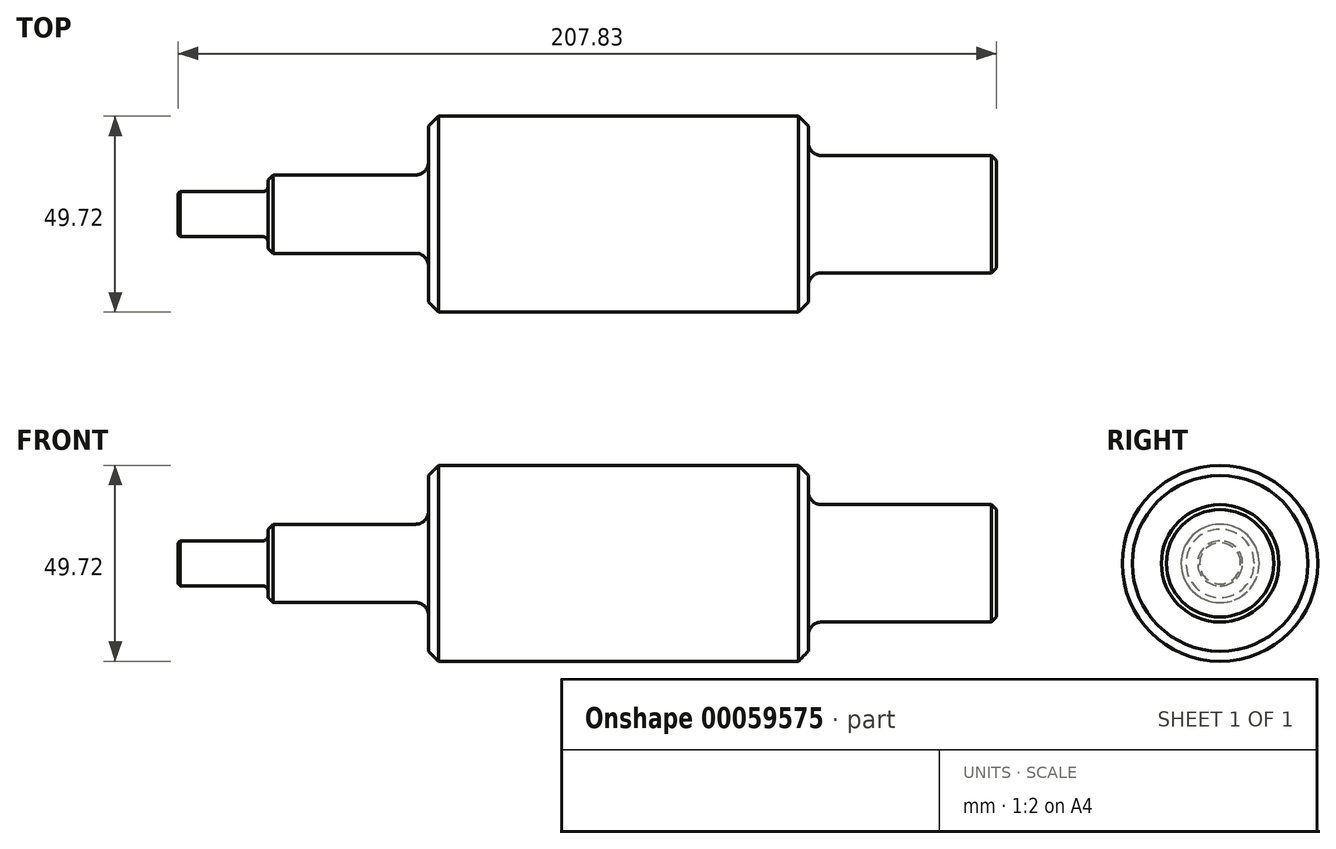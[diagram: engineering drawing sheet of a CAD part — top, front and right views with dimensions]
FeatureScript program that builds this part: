
annotation { "Feature Type Name" : "Feature", "Feature Type Description" : "" }
export const myFeature = defineFeature(function(context is Context, id is Id, definition is map)
    precondition{}
    {
        {
            var Q0;
            Q0=qCreatedBy(makeId("Front.planeOp"),FACE);
            var sketch = newSketch(context, id + "F0", { "sketchPlane" : qUnion([Q0])});
            skLineSegment(sketch, "E0", {"start": v(-95.5, 9.94) * mm, "end": v(-58.02, 9.94) * mm});
            skLineSegment(sketch, "E1", {"start": v(-54.71, 13.24) * mm, "end": v(-54.71, 24.86) * mm});
            skLineSegment(sketch, "E2", {"start": v(-54.71, 24.86) * mm, "end": v(41.78, 24.86) * mm});
            skLineSegment(sketch, "E3", {"start": v(41.78, 24.86) * mm, "end": v(41.78, 18.22) * mm});
            skLineSegment(sketch, "E4", {"start": v(45.08, 14.92) * mm, "end": v(89.53, 14.92) * mm});
            skLineSegment(sketch, "E5", {"start": v(89.53, 14.92) * mm, "end": v(89.53, 0) * mm});
            skLineSegment(sketch, "E6", {"start": v(-95.5, 9.94) * mm, "end": v(-95.5, 7.04) * mm});
            skLineSegment(sketch, "E7", {"start": v(-96.82, 5.72) * mm, "end": v(-118.3, 5.72) * mm});
            skLineSegment(sketch, "E8", {"start": v(-118.3, 5.72) * mm, "end": v(-118.3, 0) * mm});
            skLineSegment(sketch, "E9", {"start": v(-118.3, 0) * mm, "end": v(89.53, 0) * mm});
            skPoint(sketch, "E10.visualSharp", {"position": v(-95.5, 5.72) * mm});
            skArc(sketch, "E10.filletArc", {"start": v(-96.82, 5.72) * mm, "mid": v(-95.89, 6.1) * mm, "end": v(-95.5, 7.04) * mm});
            skPoint(sketch, "E11.visualSharp", {"position": v(-54.71, 9.94) * mm});
            skArc(sketch, "E11.filletArc", {"start": v(-58.02, 9.94) * mm, "mid": v(-55.68, 10.9) * mm, "end": v(-54.71, 13.24) * mm});
            skPoint(sketch, "E12.visualSharp", {"position": v(41.78, 14.92) * mm});
            skArc(sketch, "E12.filletArc", {"start": v(41.78, 18.22) * mm, "mid": v(42.75, 15.88) * mm, "end": v(45.08, 14.92) * mm});
            skSolve(sketch);
        }
        {
            var Q0;
            Q0 = qSketchRegion(id + "F0", true);
            var Q1;
            Q1=sQuery(id+"F0.wireOp",EDGE,"E7");
            var Q2;
            Q2=sQuery(id+"F0.wireOp",EDGE,"E4");
            var Q3;
            Q3=sQuery(id+"F0.wireOp",EDGE,"E0");
            var Q4;
            Q4=sQuery(id+"F0.wireOp",EDGE,"E5");
            var Q5;
            Q5=sQuery(id+"F0.wireOp",EDGE,"E2");
            var Q6;
            Q6=sQuery(id+"F0.wireOp",EDGE,"E1");
            var Q7;
            Q7=sQuery(id+"F0.wireOp",EDGE,"E6");
            var Q8;
            Q8=sQuery(id+"F0.wireOp",EDGE,"E8");
            var Q9;
            Q9=sQuery(id+"F0.wireOp",EDGE,"E3");
            var Q10;
            Q10=sQuery(id+"F0.wireOp",EDGE,"E9");
            revolve(context, id + "F1", {"entities" : qUnion([Q0]), "surfaceEntities" : qUnion([Q1, Q2, Q3, Q4, Q5, Q6, Q7, Q8, Q9]), "axis" : qUnion([Q10]), "revolveType" : RevolveType.FULL});
        }
        {
            var Q0;
            Q0=makeQuery(id+"F1.opRevolve","SWEPT_EDGE",EDGE,{"disambiguationData":[OSD([sQuery(id+"F0.wireOp",EDGE,"E2"),sQuery(id+"F0.wireOp",EDGE,"E3")])]});
            chamfer(context, id + "F2", {"entities" : qUnion([Q0]), "width" : 2.54 * mm, "tangentPropagation" : true});
        }
        {
            var Q0;
            Q0=makeQuery(id+"F1.opRevolve","SWEPT_EDGE",EDGE,{"disambiguationData":[OSD([sQuery(id+"F0.wireOp",EDGE,"E1"),sQuery(id+"F0.wireOp",EDGE,"E2")])]});
            chamfer(context, id + "F3", {"entities" : qUnion([Q0]), "width" : 2.54 * mm, "tangentPropagation" : true});
        }
        {
            var Q0;
            Q0=makeQuery(id+"F1.opRevolve","SWEPT_EDGE",EDGE,{"disambiguationData":[OSD([sQuery(id+"F0.wireOp",EDGE,"E0"),sQuery(id+"F0.wireOp",EDGE,"E6")])]});
            chamfer(context, id + "F4", {"entities" : qUnion([Q0]), "width" : 1.27 * mm, "tangentPropagation" : true});
        }
        {
            var Q0;
            Q0=makeQuery(id+"F1.opRevolve","SWEPT_EDGE",EDGE,{"disambiguationData":[OSD([sQuery(id+"F0.wireOp",EDGE,"E7"),sQuery(id+"F0.wireOp",EDGE,"E8")])]});
            chamfer(context, id + "F5", {"entities" : qUnion([Q0]), "width" : 0.5 * mm, "tangentPropagation" : true});
        }
        {
            var Q0;
            Q0=makeQuery(id+"F1.opRevolve","SWEPT_EDGE",EDGE,{"disambiguationData":[OSD([sQuery(id+"F0.wireOp",EDGE,"E4"),sQuery(id+"F0.wireOp",EDGE,"E5")])]});
            chamfer(context, id + "F6", {"entities" : qUnion([Q0]), "width" : 1.27 * mm, "tangentPropagation" : true});
        }
    });
